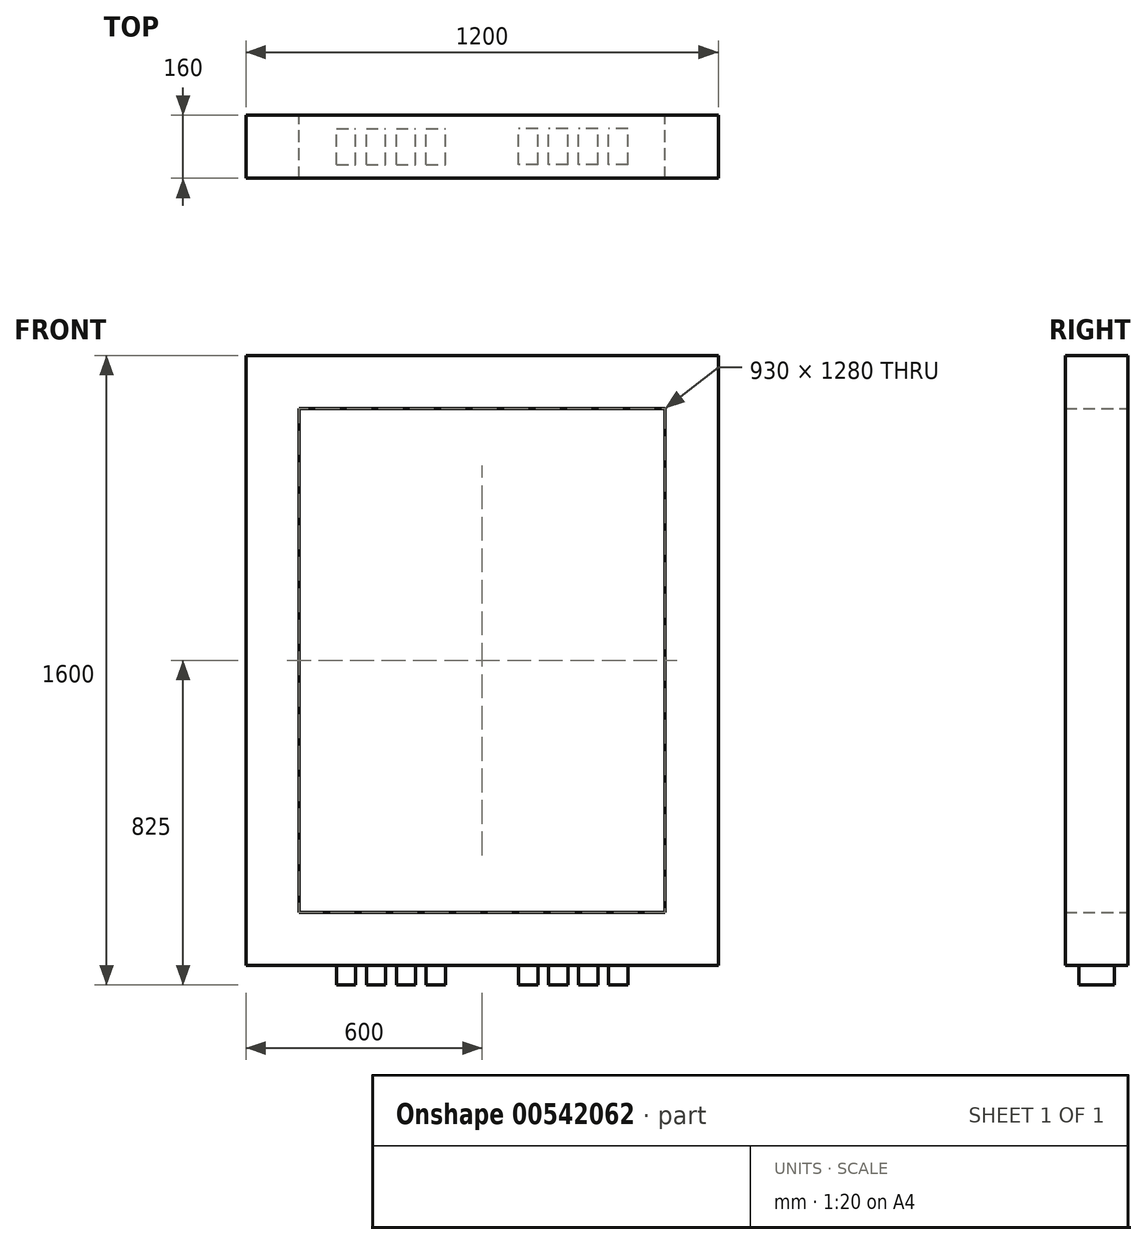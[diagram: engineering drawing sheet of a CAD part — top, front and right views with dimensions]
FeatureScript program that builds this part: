
annotation { "Feature Type Name" : "Feature", "Feature Type Description" : "" }
export const myFeature = defineFeature(function(context is Context, id is Id, definition is map)
    precondition{}
    {
        {
            var Q0;
            Q0=qCreatedBy(makeId("Front.planeOp"),FACE);
            var sketch = newSketch(context, id + "F0", { "sketchPlane" : qUnion([Q0])});
            skLineSegment(sketch, "E0.bottom", {"start": v(-600, 0) * mm, "end": v(600, 0) * mm});
            skLineSegment(sketch, "E0.top", {"start": v(-600, 1550) * mm, "end": v(600, 1550) * mm});
            skLineSegment(sketch, "E0.left", {"start": v(-600, 0) * mm, "end": v(-600, 1550) * mm});
            skLineSegment(sketch, "E0.right", {"start": v(600, 0) * mm, "end": v(600, 1550) * mm});
            skLineSegment(sketch, "E1.0", {"start": v(-465, 1415) * mm, "end": v(465, 1415) * mm});
            skLineSegment(sketch, "E1.1", {"start": v(-465, 135) * mm, "end": v(-465, 1415) * mm});
            skLineSegment(sketch, "E1.2", {"start": v(-465, 135) * mm, "end": v(465, 135) * mm});
            skLineSegment(sketch, "E1.3", {"start": v(465, 135) * mm, "end": v(465, 1415) * mm});
            skSolve(sketch);
        }
        {
            var Q0;
            Q0 = qSketchRegion(id + "F0", true);
            extrude(context, id + "F1", {"entities" : qUnion([Q0]), "endBound" : BoundingType.SYMMETRIC, "depth" : 160 * mm, "offsetDistance" : 25 * mm});
        }
        {
            var Q0;
            Q0=makeQuery(id+"F1.opExtrude","SWEPT_FACE",FACE,{"disambiguationData":[OSD([sQuery(id+"F0.wireOp",EDGE,"E0.bottom")])]});
            var sketch = newSketch(context, id + "F2", { "sketchPlane" : qUnion([Q0])});
            skLineSegment(sketch, "E2.bottom", {"start": v(-370, 45.5) * mm, "end": v(-321, 45.5) * mm});
            skLineSegment(sketch, "E2.top", {"start": v(-370, -45.5) * mm, "end": v(-321, -45.5) * mm});
            skLineSegment(sketch, "E2.left", {"start": v(-370, 45.5) * mm, "end": v(-370, -45.5) * mm});
            skLineSegment(sketch, "E2.right", {"start": v(-321, 45.5) * mm, "end": v(-321, -45.5) * mm});
            skPoint(sketch, "E3", {"position": v(-321, 0) * mm});
            skPoint(sketch, "E4.1.0.0", {"position": v(-245, 0) * mm});
            skLineSegment(sketch, "E4.1.0.1", {"start": v(-294, 45.5) * mm, "end": v(-245, 45.5) * mm});
            skLineSegment(sketch, "E4.1.0.2", {"start": v(-294, -45.5) * mm, "end": v(-245, -45.5) * mm});
            skLineSegment(sketch, "E4.1.0.3", {"start": v(-294, 45.5) * mm, "end": v(-294, -45.5) * mm});
            skLineSegment(sketch, "E4.1.0.4", {"start": v(-245, 45.5) * mm, "end": v(-245, -45.5) * mm});
            skPoint(sketch, "E4.2.0.0", {"position": v(-169, 0) * mm});
            skLineSegment(sketch, "E4.2.0.1", {"start": v(-218, 45.5) * mm, "end": v(-169, 45.5) * mm});
            skLineSegment(sketch, "E4.2.0.2", {"start": v(-218, -45.5) * mm, "end": v(-169, -45.5) * mm});
            skLineSegment(sketch, "E4.2.0.3", {"start": v(-218, 45.5) * mm, "end": v(-218, -45.5) * mm});
            skLineSegment(sketch, "E4.2.0.4", {"start": v(-169, 45.5) * mm, "end": v(-169, -45.5) * mm});
            skPoint(sketch, "E4.3.0.0", {"position": v(-93, 0) * mm});
            skLineSegment(sketch, "E4.3.0.1", {"start": v(-142, 45.5) * mm, "end": v(-93, 45.5) * mm});
            skLineSegment(sketch, "E4.3.0.2", {"start": v(-142, -45.5) * mm, "end": v(-93, -45.5) * mm});
            skLineSegment(sketch, "E4.3.0.3", {"start": v(-142, 45.5) * mm, "end": v(-142, -45.5) * mm});
            skLineSegment(sketch, "E4.3.0.4", {"start": v(-93, 45.5) * mm, "end": v(-93, -45.5) * mm});
            skLineSegment(sketch, "E4.direction1", {"start": v(-370, -45.5) * mm, "end": v(-294, -45.5) * mm, "construction": true});
            skLineSegment(sketch, "E5", {"start": v(0, -80) * mm, "end": v(0, 0) * mm, "construction": true});
            skLineSegment(sketch, "E6.MirrorCS", {"start": v(370, -45.5) * mm, "end": v(294, -45.5) * mm, "construction": true});
            skLineSegment(sketch, "E7.MirrorCS", {"start": v(370, -45.5) * mm, "end": v(321, -45.5) * mm});
            skPoint(sketch, "E8.MirrorP", {"position": v(321, 0) * mm});
            skPoint(sketch, "E9.MirrorP", {"position": v(93, 0) * mm});
            skPoint(sketch, "E10.MirrorP", {"position": v(245, 0) * mm});
            skPoint(sketch, "E11.MirrorP", {"position": v(169, 0) * mm});
            skLineSegment(sketch, "E12.MirrorCS", {"start": v(142, -45.5) * mm, "end": v(93, -45.5) * mm});
            skLineSegment(sketch, "E13.MirrorCS", {"start": v(142, 45.5) * mm, "end": v(142, -45.5) * mm});
            skLineSegment(sketch, "E14.MirrorCS", {"start": v(93, 45.5) * mm, "end": v(93, -45.5) * mm});
            skLineSegment(sketch, "E15.MirrorCS", {"start": v(370, 45.5) * mm, "end": v(321, 45.5) * mm});
            skLineSegment(sketch, "E16.MirrorCS", {"start": v(218, 45.5) * mm, "end": v(169, 45.5) * mm});
            skLineSegment(sketch, "E17.MirrorCS", {"start": v(245, 45.5) * mm, "end": v(245, -45.5) * mm});
            skLineSegment(sketch, "E18.MirrorCS", {"start": v(294, 45.5) * mm, "end": v(294, -45.5) * mm});
            skLineSegment(sketch, "E19.MirrorCS", {"start": v(294, -45.5) * mm, "end": v(245, -45.5) * mm});
            skLineSegment(sketch, "E20.MirrorCS", {"start": v(294, 45.5) * mm, "end": v(245, 45.5) * mm});
            skLineSegment(sketch, "E21.MirrorCS", {"start": v(321, 45.5) * mm, "end": v(321, -45.5) * mm});
            skLineSegment(sketch, "E22.MirrorCS", {"start": v(142, 45.5) * mm, "end": v(93, 45.5) * mm});
            skLineSegment(sketch, "E23.MirrorCS", {"start": v(370, 45.5) * mm, "end": v(370, -45.5) * mm});
            skLineSegment(sketch, "E24.MirrorCS", {"start": v(169, 45.5) * mm, "end": v(169, -45.5) * mm});
            skLineSegment(sketch, "E25.MirrorCS", {"start": v(218, -45.5) * mm, "end": v(169, -45.5) * mm});
            skLineSegment(sketch, "E26.MirrorCS", {"start": v(218, 45.5) * mm, "end": v(218, -45.5) * mm});
            skSolve(sketch);
        }
        {
            var Q0;
            Q0 = qSketchRegion(id + "F2", true);
            extrude(context, id + "F3", {"entities" : qUnion([Q0]), "depth" : 50 * mm, "offsetDistance" : 25 * mm});
        }
    });
